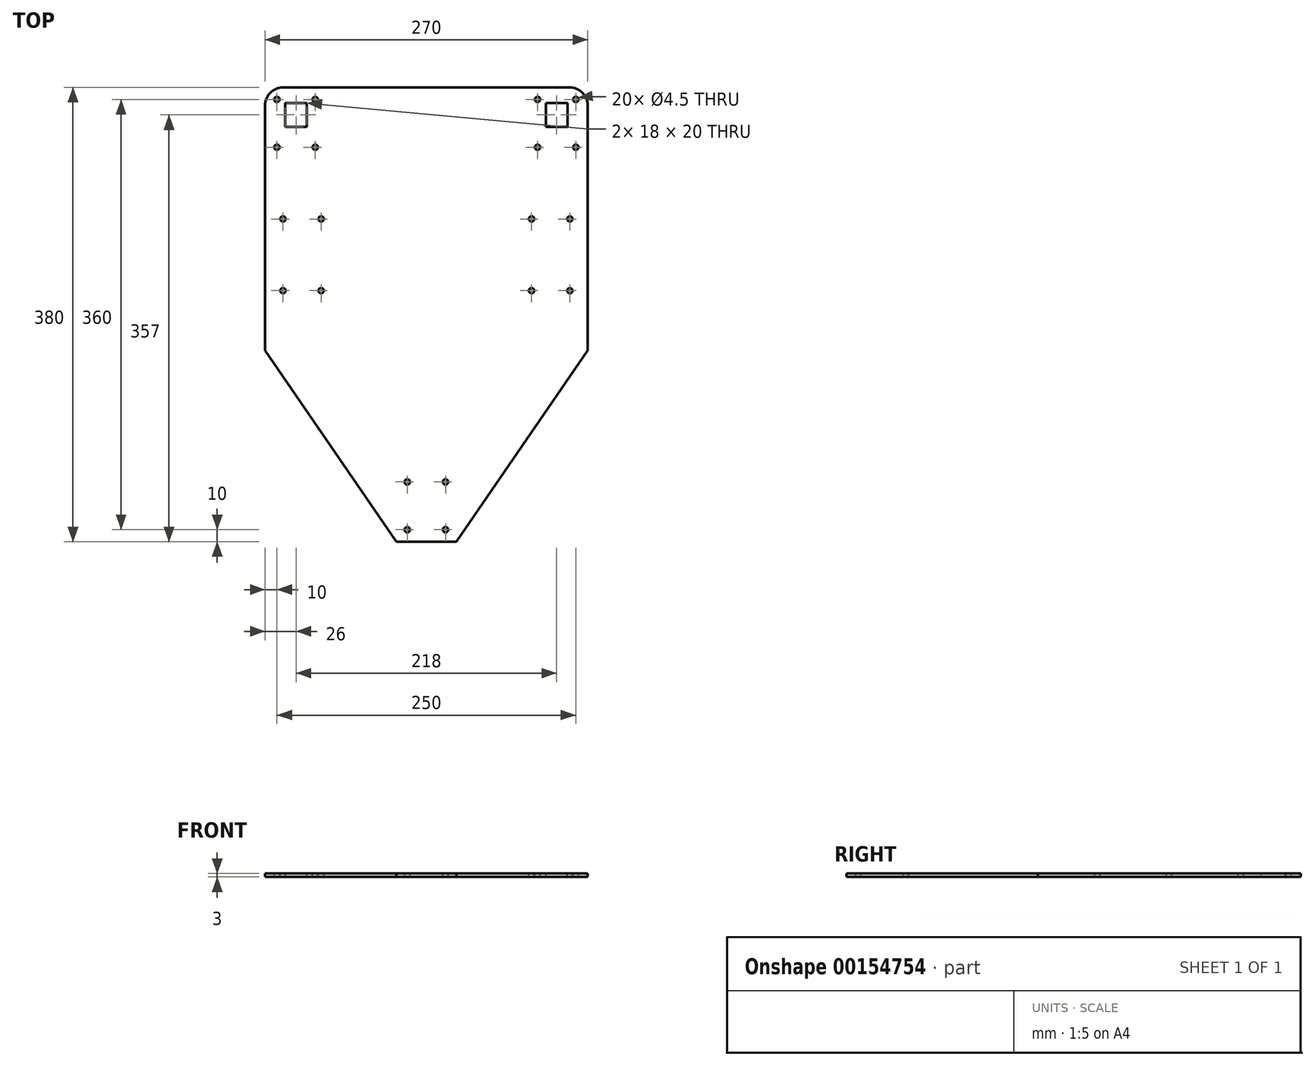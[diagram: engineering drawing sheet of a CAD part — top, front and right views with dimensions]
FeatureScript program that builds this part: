
annotation { "Feature Type Name" : "Feature", "Feature Type Description" : "" }
export const myFeature = defineFeature(function(context is Context, id is Id, definition is map)
    precondition{}
    {
        {
            var Q0;
            Q0=qCreatedBy(makeId("Top.planeOp"),FACE);
            var sketch = newSketch(context, id + "F0", { "sketchPlane" : qUnion([Q0])});
            skLineSegment(sketch, "E0.bottom", {"start": v(135, -140) * mm, "end": v(-135, -140) * mm});
            skLineSegment(sketch, "E0.top", {"start": v(135, 140) * mm, "end": v(-135, 140) * mm});
            skLineSegment(sketch, "E0.left", {"start": v(135, -140) * mm, "end": v(135, 140) * mm});
            skLineSegment(sketch, "E0.right", {"start": v(-135, -140) * mm, "end": v(-135, 140) * mm});
            skPoint(sketch, "E0.middle", {"position": v(0, 0) * mm});
            skSolve(sketch);
        }
        {
            var Q0;
            Q0 = qSketchRegion(id + "F0", true);
            extrude(context, id + "F1", {"entities" : qUnion([Q0]), "depth" : 3 * mm});
        }
        {
            var Q0;
            Q0=makeQuery(id+"F1.opExtrude","CAP_FACE",FACE,{"disambiguationData":[OSD([sQuery(id+"F0.wireOp",EDGE,"E0.bottom"),sQuery(id+"F0.wireOp",EDGE,"E0.top"),sQuery(id+"F0.wireOp",EDGE,"E0.left"),sQuery(id+"F0.wireOp",EDGE,"E0.right")])],"isStart":false});
            var sketch = newSketch(context, id + "F2", { "sketchPlane" : qUnion([Q0])});
            skLineSegment(sketch, "E1", {"start": v(0, 0) * mm, "end": v(0, -140) * mm});
            skCircle(sketch, "E2", {"center": v(-16, -130) * mm, "radius": 2.25 * mm});
            skCircle(sketch, "E3.0.1.0", {"center": v(-16, -90) * mm, "radius": 2.25 * mm});
            skCircle(sketch, "E3.1.0.0", {"center": v(16, -130) * mm, "radius": 2.25 * mm});
            skCircle(sketch, "E3.1.1.0", {"center": v(16, -90) * mm, "radius": 2.25 * mm});
            skLineSegment(sketch, "E3.direction1", {"start": v(-16, -130) * mm, "end": v(16, -130) * mm, "construction": true});
            skLineSegment(sketch, "E3.direction2", {"start": v(-16, -130) * mm, "end": v(-16, -90) * mm, "construction": true});
            skLineSegment(sketch, "E4", {"start": v(-30, 128) * mm, "end": v(30, 128) * mm});
            skLineSegment(sketch, "E5", {"start": v(-30, -6) * mm, "end": v(30, -6) * mm});
            skCircle(sketch, "E6.MirrorC", {"center": v(-16, 118) * mm, "radius": 2.25 * mm});
            skCircle(sketch, "E7.MirrorC", {"center": v(16, 118) * mm, "radius": 2.25 * mm});
            skCircle(sketch, "E8.MirrorC", {"center": v(16, 78) * mm, "radius": 2.25 * mm});
            skCircle(sketch, "E9.MirrorC", {"center": v(-16, 78) * mm, "radius": 2.25 * mm});
            skSolve(sketch);
        }
        {
            var Q0;
            Q0=makeQuery(id+"F2.imprint","IMPRINT",FACE,{"disambiguationData":[TD([[makeQuery(id+"F2.imprint","IMPRINT",EDGE,{"derivedFrom":sQuery(id+"F2.wireOp",EDGE,"E2")}),1.0]])]});
            var Q1;
            Q1=makeQuery(id+"F2.imprint","IMPRINT",FACE,{"disambiguationData":[TD([[makeQuery(id+"F2.imprint","IMPRINT",EDGE,{"derivedFrom":sQuery(id+"F2.wireOp",EDGE,"E3.0.1.0")}),1.0]])]});
            var Q2;
            Q2=makeQuery(id+"F2.imprint","IMPRINT",FACE,{"disambiguationData":[TD([[makeQuery(id+"F2.imprint","IMPRINT",EDGE,{"derivedFrom":sQuery(id+"F2.wireOp",EDGE,"E3.1.0.0")}),1.0]])]});
            var Q3;
            Q3=makeQuery(id+"F2.imprint","IMPRINT",FACE,{"disambiguationData":[TD([[makeQuery(id+"F2.imprint","IMPRINT",EDGE,{"derivedFrom":sQuery(id+"F2.wireOp",EDGE,"E3.1.1.0")}),1.0]])]});
            var Q4;
            Q4=makeQuery(id+"F2.imprint","IMPRINT",FACE,{"disambiguationData":[TD([[makeQuery(id+"F2.imprint","IMPRINT",EDGE,{"derivedFrom":sQuery(id+"F2.wireOp",EDGE,"E7.MirrorC")}),-1.0]])]});
            var Q5;
            Q5=makeQuery(id+"F2.imprint","IMPRINT",FACE,{"disambiguationData":[TD([[makeQuery(id+"F2.imprint","IMPRINT",EDGE,{"derivedFrom":sQuery(id+"F2.wireOp",EDGE,"E8.MirrorC")}),-1.0]])]});
            var Q6;
            Q6=makeQuery(id+"F2.imprint","IMPRINT",FACE,{"disambiguationData":[TD([[makeQuery(id+"F2.imprint","IMPRINT",EDGE,{"derivedFrom":sQuery(id+"F2.wireOp",EDGE,"E9.MirrorC")}),-1.0]])]});
            var Q7;
            Q7=makeQuery(id+"F2.imprint","IMPRINT",FACE,{"disambiguationData":[TD([[makeQuery(id+"F2.imprint","IMPRINT",EDGE,{"derivedFrom":sQuery(id+"F2.wireOp",EDGE,"E6.MirrorC")}),-1.0]])]});
            extrude(context, id + "F3", {"entities" : qUnion([Q0, Q1, Q2, Q3, Q4, Q5, Q6, Q7]), "operationType" : NewBodyOperationType.REMOVE, "endBound" : BoundingType.THROUGH_ALL, "oppositeDirection" : true, "depth" : 25 * mm});
        }
        {
            var Q0;
            Q0=makeQuery(id+"F1.opExtrude","CAP_FACE",FACE,{"disambiguationData":[OSD([sQuery(id+"F0.wireOp",EDGE,"E0.bottom"),sQuery(id+"F0.wireOp",EDGE,"E0.top"),sQuery(id+"F0.wireOp",EDGE,"E0.left"),sQuery(id+"F0.wireOp",EDGE,"E0.right")])],"isStart":false});
            var sketch = newSketch(context, id + "F4", { "sketchPlane" : qUnion([Q0])});
            skLineSegment(sketch, "E10", {"start": v(-135, 0) * mm, "end": v(135, 0) * mm});
            skLineSegment(sketch, "E11", {"start": v(0, 0) * mm, "end": v(0, 156.1) * mm});
            skCircle(sketch, "E12", {"center": v(-120, 70) * mm, "radius": 2.25 * mm});
            skCircle(sketch, "E13.0.1.0", {"center": v(-120, 130) * mm, "radius": 2.25 * mm});
            skCircle(sketch, "E13.1.0.0", {"center": v(-88, 70) * mm, "radius": 2.25 * mm});
            skCircle(sketch, "E13.1.1.0", {"center": v(-88, 130) * mm, "radius": 2.25 * mm});
            skLineSegment(sketch, "E13.direction1", {"start": v(-120, 70) * mm, "end": v(-88, 70) * mm, "construction": true});
            skLineSegment(sketch, "E13.direction2", {"start": v(-120, 70) * mm, "end": v(-120, 130) * mm, "construction": true});
            skCircle(sketch, "E14.MirrorC", {"center": v(120, 130) * mm, "radius": 2.25 * mm});
            skCircle(sketch, "E15.MirrorC", {"center": v(88, 130) * mm, "radius": 2.25 * mm});
            skCircle(sketch, "E16.MirrorC", {"center": v(88, 70) * mm, "radius": 2.25 * mm});
            skCircle(sketch, "E17.MirrorC", {"center": v(120, 70) * mm, "radius": 2.25 * mm});
            skSolve(sketch);
        }
        {
            var Q0;
            Q0 = qSketchRegion(id + "F4", true);
            extrude(context, id + "F5", {"entities" : qUnion([Q0]), "operationType" : NewBodyOperationType.REMOVE, "endBound" : BoundingType.THROUGH_ALL, "oppositeDirection" : true, "depth" : 25 * mm});
        }
        {
            var Q0;
            Q0=makeQuery(id+"F1.opExtrude","CAP_FACE",FACE,{"disambiguationData":[OSD([sQuery(id+"F0.wireOp",EDGE,"E0.bottom"),sQuery(id+"F0.wireOp",EDGE,"E0.top"),sQuery(id+"F0.wireOp",EDGE,"E0.left"),sQuery(id+"F0.wireOp",EDGE,"E0.right")])],"isStart":false});
            var sketch = newSketch(context, id + "F6", { "sketchPlane" : qUnion([Q0])});
            skLineSegment(sketch, "E18", {"start": v(-25, -140) * mm, "end": v(-135, 20) * mm});
            skLineSegment(sketch, "E19", {"start": v(-135, 20) * mm, "end": v(-135, -140) * mm});
            skLineSegment(sketch, "E20", {"start": v(-135, -140) * mm, "end": v(-25, -140) * mm});
            skLineSegment(sketch, "E21", {"start": v(0, -140) * mm, "end": v(0, 140) * mm});
            skLineSegment(sketch, "E22.MirrorCS", {"start": v(25, -140) * mm, "end": v(135, 20) * mm});
            skLineSegment(sketch, "E23.MirrorCS", {"start": v(135, 20) * mm, "end": v(135, -140) * mm});
            skLineSegment(sketch, "E24.MirrorCS", {"start": v(135, -140) * mm, "end": v(25, -140) * mm});
            skSolve(sketch);
        }
        {
            var Q0;
            Q0 = qSketchRegion(id + "F6", true);
            extrude(context, id + "F7", {"entities" : qUnion([Q0]), "operationType" : NewBodyOperationType.REMOVE, "endBound" : BoundingType.THROUGH_ALL, "oppositeDirection" : true, "depth" : 25 * mm});
        }
        {
            var Q0;
            Q0=makeQuery(id+"F1.opExtrude","SWEPT_FACE",FACE,{"disambiguationData":[OSD([sQuery(id+"F0.wireOp",EDGE,"E0.top")])]});
            extrude(context, id + "F8", {"entities" : qUnion([Q0]), "operationType" : NewBodyOperationType.ADD, "depth" : 100 * mm});
        }
        {
            var Q0;
            {var subQ0=sQuery(id+"F0.wireOp",EDGE,"E0.top");Q0=makeQuery(id+"F8.boolean.opBoolean","MERGE",FACE,{"derivedFrom":[makeQuery(id+"F1.opExtrude","CAP_FACE",FACE,{"disambiguationData":[OSD([sQuery(id+"F0.wireOp",EDGE,"E0.bottom"),subQ0,sQuery(id+"F0.wireOp",EDGE,"E0.left"),sQuery(id+"F0.wireOp",EDGE,"E0.right")])],"isStart":false}),makeQuery(id+"F8.opExtrude","SWEPT_FACE",FACE,{"disambiguationData":[OSD([subQ0]),TDD([makeQuery(id+"F1.opExtrude","CAP_EDGE",EDGE,{"disambiguationData":[OSD([subQ0])],"isStart":false})])]})]});}
            var sketch = newSketch(context, id + "F9", { "sketchPlane" : qUnion([Q0])});
            skCircle(sketch, "E25", {"center": v(125, 230) * mm, "radius": 2.25 * mm});
            skCircle(sketch, "E26.0.1.0", {"center": v(125, 190) * mm, "radius": 2.25 * mm});
            skCircle(sketch, "E26.1.0.0", {"center": v(93, 230) * mm, "radius": 2.25 * mm});
            skCircle(sketch, "E26.1.1.0", {"center": v(93, 190) * mm, "radius": 2.25 * mm});
            skLineSegment(sketch, "E26.direction1", {"start": v(125, 230) * mm, "end": v(93, 230) * mm, "construction": true});
            skLineSegment(sketch, "E26.direction2", {"start": v(125, 230) * mm, "end": v(125, 190) * mm, "construction": true});
            skCircle(sketch, "E27.MirrorC", {"center": v(-93, 230) * mm, "radius": 2.25 * mm});
            skCircle(sketch, "E28.MirrorC", {"center": v(-93, 190) * mm, "radius": 2.25 * mm});
            skCircle(sketch, "E29.MirrorC", {"center": v(-125, 190) * mm, "radius": 2.25 * mm});
            skCircle(sketch, "E30.MirrorC", {"center": v(-125, 230) * mm, "radius": 2.25 * mm});
            skSolve(sketch);
        }
        {
            var Q0;
            Q0 = qSketchRegion(id + "F9", true);
            extrude(context, id + "F10", {"entities" : qUnion([Q0]), "operationType" : NewBodyOperationType.REMOVE, "endBound" : BoundingType.THROUGH_ALL, "oppositeDirection" : true, "depth" : 25 * mm});
        }
        {
            var Q0;
            {var subQ0=sQuery(id+"F0.wireOp",EDGE,"E0.top");Q0=makeQuery(id+"F8.boolean.opBoolean","MERGE",FACE,{"derivedFrom":[makeQuery(id+"F1.opExtrude","CAP_FACE",FACE,{"disambiguationData":[OSD([sQuery(id+"F0.wireOp",EDGE,"E0.bottom"),subQ0,sQuery(id+"F0.wireOp",EDGE,"E0.left"),sQuery(id+"F0.wireOp",EDGE,"E0.right")])],"isStart":false}),makeQuery(id+"F8.opExtrude","SWEPT_FACE",FACE,{"disambiguationData":[OSD([subQ0]),TDD([makeQuery(id+"F1.opExtrude","CAP_EDGE",EDGE,{"disambiguationData":[OSD([subQ0])],"isStart":false})])]})]});}
            var sketch = newSketch(context, id + "F11", { "sketchPlane" : qUnion([Q0])});
            skLineSegment(sketch, "E31.bottom", {"start": v(-100, 207) * mm, "end": v(-118, 207) * mm});
            skLineSegment(sketch, "E31.top", {"start": v(-100, 227) * mm, "end": v(-118, 227) * mm});
            skLineSegment(sketch, "E31.left", {"start": v(-100, 207) * mm, "end": v(-100, 227) * mm});
            skLineSegment(sketch, "E31.right", {"start": v(-118, 207) * mm, "end": v(-118, 227) * mm});
            skPoint(sketch, "E31.middle", {"position": v(-109, 217) * mm});
            skLineSegment(sketch, "E32.MirrorCS", {"start": v(100, 227) * mm, "end": v(118, 227) * mm});
            skLineSegment(sketch, "E33.MirrorCS", {"start": v(100, 207) * mm, "end": v(100, 227) * mm});
            skLineSegment(sketch, "E34.MirrorCS", {"start": v(100, 207) * mm, "end": v(118, 207) * mm});
            skLineSegment(sketch, "E35.MirrorCS", {"start": v(118, 207) * mm, "end": v(118, 227) * mm});
            skSolve(sketch);
        }
        {
            var Q0;
            Q0 = qSketchRegion(id + "F11", true);
            extrude(context, id + "F12", {"entities" : qUnion([Q0]), "operationType" : NewBodyOperationType.REMOVE, "endBound" : BoundingType.THROUGH_ALL, "oppositeDirection" : true, "depth" : 25 * mm});
        }
        {
            var Q0;
            Q0=makeQuery(id+"F7.boolean.opBoolean","COPY",EDGE,{"derivedFrom":makeQuery(id+"F7.opExtrude","SWEPT_EDGE",EDGE,{"disambiguationData":[OSD([sQuery(id+"F0.wireOp",EDGE,"E0.bottom"),sQuery(id+"F6.wireOp",EDGE,"E18"),sQuery(id+"F6.wireOp",EDGE,"E20")])]})});
            var Q1;
            Q1=makeQuery(id+"F7.boolean.opBoolean","COPY",EDGE,{"derivedFrom":makeQuery(id+"F7.opExtrude","SWEPT_EDGE",EDGE,{"disambiguationData":[OSD([sQuery(id+"F0.wireOp",EDGE,"E0.bottom"),sQuery(id+"F6.wireOp",EDGE,"E22.MirrorCS"),sQuery(id+"F6.wireOp",EDGE,"E24.MirrorCS")])]})});
            var Q2;
            Q2=makeQuery(id+"F7.boolean.opBoolean","COPY",EDGE,{"derivedFrom":makeQuery(id+"F7.opExtrude","SWEPT_EDGE",EDGE,{"disambiguationData":[OSD([sQuery(id+"F0.wireOp",EDGE,"E0.left"),sQuery(id+"F6.wireOp",EDGE,"E22.MirrorCS"),sQuery(id+"F6.wireOp",EDGE,"E23.MirrorCS")])]})});
            var Q3;
            Q3=makeQuery(id+"F8.opExtrude","CAP_EDGE",EDGE,{"disambiguationData":[OSD([sQuery(id+"F0.wireOp",EDGE,"E0.top"),sQuery(id+"F0.wireOp",EDGE,"E0.left")])],"isStart":false});
            var Q4;
            Q4=makeQuery(id+"F8.opExtrude","CAP_EDGE",EDGE,{"disambiguationData":[OSD([sQuery(id+"F0.wireOp",EDGE,"E0.top"),sQuery(id+"F0.wireOp",EDGE,"E0.right")])],"isStart":false});
            var Q5;
            Q5=makeQuery(id+"F7.boolean.opBoolean","COPY",EDGE,{"derivedFrom":makeQuery(id+"F7.opExtrude","SWEPT_EDGE",EDGE,{"disambiguationData":[OSD([sQuery(id+"F0.wireOp",EDGE,"E0.right"),sQuery(id+"F6.wireOp",EDGE,"E18"),sQuery(id+"F6.wireOp",EDGE,"E19")])]})});
            fillet(context, id + "F13", {"entities" : qUnion([Q0, Q1, Q2, Q3, Q4, Q5]), "radius" : 15 * mm, "tangentPropagation" : true, "allowEdgeOverflow" : false});
        }
    });
